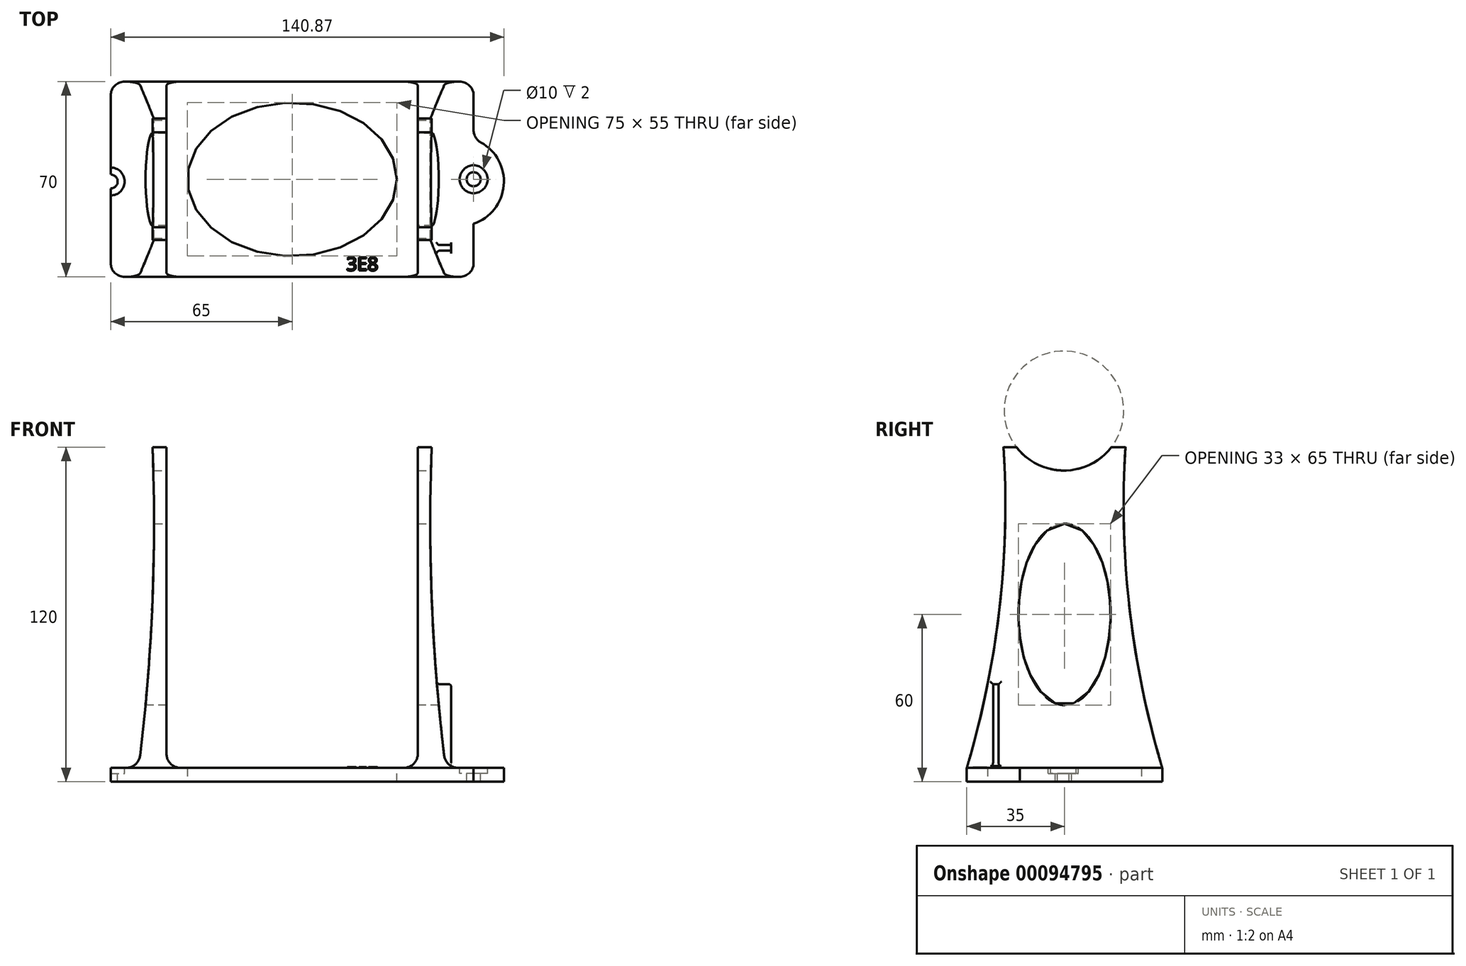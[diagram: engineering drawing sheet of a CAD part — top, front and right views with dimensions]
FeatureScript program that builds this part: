
annotation { "Feature Type Name" : "Feature", "Feature Type Description" : "" }
export const myFeature = defineFeature(function(context is Context, id is Id, definition is map)
    precondition{}
    {
        {
            var Q0;
            Q0=qCreatedBy(makeId("Front.planeOp"),FACE);
            var sketch = newSketch(context, id + "F0", { "sketchPlane" : qUnion([Q0])});
            skLineSegment(sketch, "E0", {"start": v(-65, 0) * mm, "end": v(65, 0) * mm});
            skLineSegment(sketch, "E1", {"start": v(0, 0) * mm, "end": v(0, 120) * mm, "construction": true});
            skLineSegment(sketch, "E2", {"start": v(-65, 0) * mm, "end": v(-65, 5) * mm});
            skLineSegment(sketch, "E3", {"start": v(-65, 5) * mm, "end": v(-55, 5) * mm});
            skLineSegment(sketch, "E4", {"start": v(-45, 120) * mm, "end": v(45, 120) * mm, "construction": true});
            skLineSegment(sketch, "E5", {"start": v(-45, 120) * mm, "end": v(-45, 5) * mm});
            skLineSegment(sketch, "E6", {"start": v(-45, 5) * mm, "end": v(0, 5) * mm});
            skLineSegment(sketch, "E7", {"start": v(-45, 120) * mm, "end": v(-50, 120) * mm});
            skArc(sketch, "E8", {"start": v(-55, 5) * mm, "mid": v(-50.13, 62.4) * mm, "end": v(-50, 120) * mm});
            skLineSegment(sketch, "E9.MirrorCS", {"start": v(45, 5) * mm, "end": v(0, 5) * mm});
            skLineSegment(sketch, "E10.MirrorCS", {"start": v(45, 120) * mm, "end": v(45, 5) * mm});
            skLineSegment(sketch, "E11.MirrorCS", {"start": v(45, 120) * mm, "end": v(50, 120) * mm});
            skArc(sketch, "E12.MirrorCS", {"start": v(55, 5) * mm, "mid": v(50.13, 62.4) * mm, "end": v(50, 120) * mm});
            skLineSegment(sketch, "E13.MirrorCS", {"start": v(65, 5) * mm, "end": v(55, 5) * mm});
            skLineSegment(sketch, "E14.MirrorCS", {"start": v(65, 0) * mm, "end": v(65, 5) * mm});
            skSolve(sketch);
        }
        {
            var Q0;
            Q0 = qSketchRegion(id + "F0", true);
            extrude(context, id + "F1", {"entities" : qUnion([Q0]), "endBound" : BoundingType.SYMMETRIC, "depth" : 70 * mm});
        }
        {
            var Q0;
            Q0=qCreatedBy(makeId("Right.planeOp"),FACE);
            var sketch = newSketch(context, id + "F2", { "sketchPlane" : qUnion([Q0])});
            skLineSegment(sketch, "E15.0", {"start": v(-35, 120) * mm, "end": v(35, 120) * mm, "construction": true});
            skPoint(sketch, "E16", {"position": v(0, 120) * mm});
            skArc(sketch, "E17", {"start": v(-21.63, 132.72) * mm, "mid": v(0.07, 111.58) * mm, "end": v(21.2, 133.28) * mm});
            skLineSegment(sketch, "E18", {"start": v(-0.21, 133) * mm, "end": v(0, 120) * mm, "construction": true});
            skLineSegment(sketch, "E19", {"start": v(21.2, 133.28) * mm, "end": v(-21.63, 132.72) * mm});
            skPoint(sketch, "E20", {"position": v(16.81, 120) * mm});
            skLineSegment(sketch, "E21", {"start": v(16.81, 120) * mm, "end": v(21.81, 120) * mm});
            skPoint(sketch, "E22.0", {"position": v(35, 5) * mm});
            skArc(sketch, "E23", {"start": v(21.81, 120) * mm, "mid": v(23.32, 61.92) * mm, "end": v(35, 5) * mm});
            skLineSegment(sketch, "E24", {"start": v(0, 120) * mm, "end": v(0, 0) * mm, "construction": true});
            skEllipse(sketch, "E25", {"center": v(0, 60) * mm, "majorRadius": 32.5 * mm, "minorRadius": 16.5 * mm, "majorAxis": v(0, 1)});
            skLineSegment(sketch, "E26", {"start": v(21.81, 120) * mm, "end": v(35, 120) * mm});
            skLineSegment(sketch, "E27", {"start": v(35, 120) * mm, "end": v(35, 5) * mm});
            skArc(sketch, "E28.MirrorCS", {"start": v(-21.81, 120) * mm, "mid": v(-23.32, 61.92) * mm, "end": v(-35, 5) * mm});
            skLineSegment(sketch, "E29.MirrorCS", {"start": v(-21.81, 120) * mm, "end": v(-35, 120) * mm});
            skLineSegment(sketch, "E30.MirrorCS", {"start": v(-35, 120) * mm, "end": v(-35, 5) * mm});
            skSolve(sketch);
        }
        {
            var Q0;
            Q0 = qSketchRegion(id + "F2", true);
            extrude(context, id + "F3", {"entities" : qUnion([Q0]), "operationType" : NewBodyOperationType.REMOVE, "endBound" : BoundingType.THROUGH_ALL, "oppositeDirection" : true, "depth" : 25 * mm, "hasSecondDirection" : true, "secondDirectionBound" : SecondDirectionBoundingType.THROUGH_ALL, "secondDirectionOppositeDirection" : false, "secondDirectionDepth" : 25 * mm});
        }
        {
            var Q0;
            Q0=makeQuery(id+"F1.opExtrude","SWEPT_FACE",FACE,{"disambiguationData":[OSD([sQuery(id+"F0.wireOp",EDGE,"E6"),sQuery(id+"F0.wireOp",EDGE,"E9.MirrorCS")])]});
            var sketch = newSketch(context, id + "F4", { "sketchPlane" : qUnion([Q0])});
            skLineSegment(sketch, "E31.0", {"start": v(65, -35) * mm, "end": v(65, 35) * mm, "construction": true});
            skArc(sketch, "E32", {"start": v(65, -15.96) * mm, "mid": v(75.87, -0.8) * mm, "end": v(65, 14.35) * mm});
            skLineSegment(sketch, "E33", {"start": v(65, -15.96) * mm, "end": v(65, 14.35) * mm});
            skPoint(sketch, "E34", {"position": v(65, 0) * mm});
            skLineSegment(sketch, "E35", {"start": v(0, -6.05) * mm, "end": v(0, 5.95) * mm, "construction": true});
            skArc(sketch, "E36.MirrorCS", {"start": v(-65, -15.96) * mm, "mid": v(-75.87, -0.8) * mm, "end": v(-65, 14.35) * mm});
            skLineSegment(sketch, "E37.MirrorCS", {"start": v(-65, -15.96) * mm, "end": v(-65, 14.35) * mm});
            skPoint(sketch, "E38", {"position": v(-65, -0.8) * mm});
            skEllipse(sketch, "E39", {"center": v(0, 0) * mm, "majorRadius": 37.5 * mm, "minorRadius": 27.5 * mm, "majorAxis": v(1, 0)});
            skSolve(sketch);
        }
        {
            var Q0;
            Q0=makeQuery(id+"F4.imprint","IMPRINT",FACE,{"disambiguationData":[TD([[makeQuery(id+"F4.imprint","IMPRINT",EDGE,{"derivedFrom":sQuery(id+"F4.wireOp",EDGE,"E39")}),1.0]])]});
            extrude(context, id + "F5", {"entities" : qUnion([Q0]), "operationType" : NewBodyOperationType.REMOVE, "endBound" : BoundingType.THROUGH_ALL, "oppositeDirection" : true, "depth" : 25 * mm});
        }
        {
            var Q0;
            Q0=makeQuery(id+"F4.imprint","IMPRINT",FACE,{"disambiguationData":[TD([[makeQuery(id+"F4.imprint","IMPRINT",EDGE,{"derivedFrom":sQuery(id+"F4.wireOp",EDGE,"E32")}),1.0]])]});
            var Q1;
            Q1=makeQuery(id+"F4.imprint","IMPRINT",FACE,{"disambiguationData":[TD([[makeQuery(id+"F4.imprint","IMPRINT",EDGE,{"derivedFrom":sQuery(id+"F4.wireOp",EDGE,"E36.MirrorCS")}),-1.0]])]});
            extrude(context, id + "F6", {"entities" : qUnion([Q0, Q1]), "operationType" : NewBodyOperationType.ADD, "oppositeDirection" : true, "depth" : 5 * mm});
        }
        {
            var Q0;
            Q0=sQuery(id+"F4.wireOp",VERTEX,"E34");
            var Q1;
            Q1=sQuery(id+"F4.wireOp",VERTEX,"E38");
            var Q2;
            Q2=makeQuery(id+"F1.opExtrude","SWEPT_BODY",BODY,{"disambiguationData":[OSD([sQuery(id+"F0.wireOp",EDGE,"E0"),sQuery(id+"F0.wireOp",EDGE,"E2"),sQuery(id+"F0.wireOp",EDGE,"E3"),sQuery(id+"F0.wireOp",EDGE,"E5"),sQuery(id+"F0.wireOp",EDGE,"E6"),sQuery(id+"F0.wireOp",EDGE,"E7"),sQuery(id+"F0.wireOp",EDGE,"E8"),sQuery(id+"F0.wireOp",EDGE,"E9.MirrorCS"),sQuery(id+"F0.wireOp",EDGE,"E10.MirrorCS"),sQuery(id+"F0.wireOp",EDGE,"E11.MirrorCS"),sQuery(id+"F0.wireOp",EDGE,"E12.MirrorCS"),sQuery(id+"F0.wireOp",EDGE,"E13.MirrorCS"),sQuery(id+"F0.wireOp",EDGE,"E14.MirrorCS")])]});
            hole(context, id + "F7", {"style" : HoleStyle.C_BORE, "endStyle" : HoleEndStyle.THROUGH, "holeDiameter" : 5 * mm, "cBoreDiameter" : 10 * mm, "cBoreDepth" : 2 * mm, "locations" : qUnion([Q0, Q1]), "scope" : qUnion([Q2]), "isTappedThrough" : true});
        }
        {
            var Q0;
            Q0=makeQuery(id+"F1.opExtrude","CAP_EDGE",EDGE,{"disambiguationData":[OSD([sQuery(id+"F0.wireOp",EDGE,"E14.MirrorCS")])],"isStart":true});
            var Q1;
            Q1=makeQuery(id+"F1.opExtrude","CAP_EDGE",EDGE,{"disambiguationData":[OSD([sQuery(id+"F0.wireOp",EDGE,"E2")])],"isStart":true});
            var Q2;
            Q2=makeQuery(id+"F1.opExtrude","CAP_EDGE",EDGE,{"disambiguationData":[OSD([sQuery(id+"F0.wireOp",EDGE,"E2")])],"isStart":false});
            var Q3;
            Q3=makeQuery(id+"F1.opExtrude","CAP_EDGE",EDGE,{"disambiguationData":[OSD([sQuery(id+"F0.wireOp",EDGE,"E14.MirrorCS")])],"isStart":false});
            var Q4;
            {var subQ0=sQuery(id+"F4.wireOp",EDGE,"E33");var subQ1=sQuery(id+"F4.wireOp",EDGE,"E32");Q4=makeQuery(id+"F6.opExtrude","SWEPT_EDGE",EDGE,{"disambiguationData":[OSD([subQ1,subQ0]),TDD([makeQuery(id+"F4.imprint","INTERSECT",VERTEX,{"disambiguationData":[OD(0.0)],"derivedFrom":[subQ1,subQ0]})])]});}
            var Q5;
            {var subQ0=sQuery(id+"F4.wireOp",EDGE,"E33");var subQ1=sQuery(id+"F4.wireOp",EDGE,"E32");Q5=makeQuery(id+"F6.opExtrude","SWEPT_EDGE",EDGE,{"disambiguationData":[OSD([subQ1,subQ0]),TDD([makeQuery(id+"F4.imprint","INTERSECT",VERTEX,{"disambiguationData":[OD(1.0)],"derivedFrom":[subQ1,subQ0]})])]});}
            var Q6;
            {var subQ0=sQuery(id+"F4.wireOp",EDGE,"E37.MirrorCS");var subQ1=sQuery(id+"F4.wireOp",EDGE,"E36.MirrorCS");Q6=makeQuery(id+"F6.opExtrude","SWEPT_EDGE",EDGE,{"disambiguationData":[OSD([subQ1,subQ0]),TDD([makeQuery(id+"F4.imprint","INTERSECT",VERTEX,{"disambiguationData":[OD(1.0)],"derivedFrom":[subQ1,subQ0]})])]});}
            var Q7;
            {var subQ0=sQuery(id+"F4.wireOp",EDGE,"E37.MirrorCS");var subQ1=sQuery(id+"F4.wireOp",EDGE,"E36.MirrorCS");Q7=makeQuery(id+"F6.opExtrude","SWEPT_EDGE",EDGE,{"disambiguationData":[OSD([subQ1,subQ0]),TDD([makeQuery(id+"F4.imprint","INTERSECT",VERTEX,{"disambiguationData":[OD(0.0)],"derivedFrom":[subQ1,subQ0]})])]});}
            var Q8;
            Q8=makeQuery(id+"F1.opExtrude","SWEPT_EDGE",EDGE,{"disambiguationData":[OSD([sQuery(id+"F0.wireOp",EDGE,"E12.MirrorCS"),sQuery(id+"F0.wireOp",EDGE,"E13.MirrorCS")])]});
            var Q9;
            Q9=makeQuery(id+"F1.opExtrude","SWEPT_EDGE",EDGE,{"disambiguationData":[OSD([sQuery(id+"F0.wireOp",EDGE,"E3"),sQuery(id+"F0.wireOp",EDGE,"E8")])]});
            var Q10;
            Q10=makeQuery(id+"F1.opExtrude","SWEPT_EDGE",EDGE,{"disambiguationData":[OSD([sQuery(id+"F0.wireOp",EDGE,"E9.MirrorCS"),sQuery(id+"F0.wireOp",EDGE,"E10.MirrorCS")])]});
            var Q11;
            Q11=makeQuery(id+"F1.opExtrude","SWEPT_EDGE",EDGE,{"disambiguationData":[OSD([sQuery(id+"F0.wireOp",EDGE,"E5"),sQuery(id+"F0.wireOp",EDGE,"E6")])]});
            fillet(context, id + "F8", {"entities" : qUnion([Q0, Q1, Q2, Q3, Q4, Q5, Q6, Q7, Q8, Q9, Q10, Q11]), "radius" : 5 * mm, "tangentPropagation" : true, "allowEdgeOverflow" : false});
        }
        {
            var Q0;
            Q0=makeQuery(id+"F4.imprint","IMPRINT",FACE,{"disambiguationData":[TD([[makeQuery(id+"F4.imprint","IMPRINT",EDGE,{"derivedFrom":sQuery(id+"F4.wireOp",EDGE,"E39")}),-1.0]])]});
            var sketch = newSketch(context, id + "F9", { "sketchPlane" : qUnion([Q0])});
            skText(sketch, "E40", { "text": "3E8", "fontName": "OpenSans-Regular.ttf"});
            const initialGuessF9  = {"E40": [0.0194, -0.03273, 1, 0, 0.00484]};
            skSetInitialGuess(sketch, initialGuessF9);
            skSolve(sketch);
        }
        {
            var Q0;
            Q0 = qSketchRegion(id + "F9", true);
            extrude(context, id + "F10", {"entities" : qUnion([Q0]), "operationType" : NewBodyOperationType.ADD, "depth" : .3 * mm});
        }
        {
            var Q0;
            Q0=qCreatedBy(makeId("Right.planeOp"),FACE);
            cPlane(context, id + "F11", {"entities" : qUnion([Q0]), "cplaneType" : CPlaneType.OFFSET, "offset" : 57 * mm, "width" : 150 * mm, "height" : 150 * mm});
        }
        {
            var Q0;
            Q0=qCreatedBy(id+"F11.planeOp",FACE);
            var sketch = newSketch(context, id + "F12", { "sketchPlane" : qUnion([Q0])});
            skLineSegment(sketch, "E41.0.1", {"start": v(35, 5) * mm, "end": v(-35, 5) * mm, "construction": true});
            skLineSegment(sketch, "E41.0.3", {"start": v(-35, 5) * mm, "end": v(-30, 5) * mm, "construction": true});
            skLineSegment(sketch, "E41.0.4", {"start": v(-30, 5) * mm, "end": v(-19.2, 5) * mm, "construction": true});
            skLineSegment(sketch, "E41.0.5", {"start": v(-19.2, 5) * mm, "end": v(-14.82, 5) * mm, "construction": true});
            skLineSegment(sketch, "E41.0.6", {"start": v(-14.82, 5) * mm, "end": v(13.21, 5) * mm, "construction": true});
            skLineSegment(sketch, "E41.0.7", {"start": v(13.21, 5) * mm, "end": v(17.6, 5) * mm, "construction": true});
            skLineSegment(sketch, "E41.0.8", {"start": v(17.6, 5) * mm, "end": v(30, 5) * mm, "construction": true});
            skLineSegment(sketch, "E41.0.9", {"start": v(30, 5) * mm, "end": v(35, 5) * mm, "construction": true});
            skLineSegment(sketch, "E42", {"start": v(-35, 5) * mm, "end": v(-24.6, 5) * mm, "construction": true});
            skLineSegment(sketch, "E43", {"start": v(-24.6, 5) * mm, "end": v(-24.6, 20) * mm, "construction": true});
            skLineSegment(sketch, "E44.bottom", {"start": v(-25.6, 5) * mm, "end": v(-23.6, 5) * mm});
            skLineSegment(sketch, "E44.top", {"start": v(-25.6, 35) * mm, "end": v(-23.6, 35) * mm});
            skLineSegment(sketch, "E44.left", {"start": v(-25.6, 5) * mm, "end": v(-25.6, 35) * mm});
            skLineSegment(sketch, "E44.right", {"start": v(-23.6, 5) * mm, "end": v(-23.6, 35) * mm});
            skPoint(sketch, "E44.middle", {"position": v(-24.6, 20) * mm});
            skSolve(sketch);
        }
        {
            var Q0;
            Q0 = qSketchRegion(id + "F12", true);
            extrude(context, id + "F13", {"entities" : qUnion([Q0]), "operationType" : NewBodyOperationType.ADD, "oppositeDirection" : true, "depth" : 5.5 * mm});
        }
        {
            var Q0;
            Q0=makeQuery(id+"F13.opExtrude","CAP_EDGE",EDGE,{"disambiguationData":[OSD([sQuery(id+"F12.wireOp",EDGE,"E44.top")])],"isStart":true});
            var Q1;
            Q1=makeQuery(id+"F13.boolean.opBoolean","INTERSECT",EDGE,{"derivedFrom":[makeQuery(id+"F1.opExtrude","SWEPT_FACE",FACE,{"disambiguationData":[OSD([sQuery(id+"F0.wireOp",EDGE,"E12.MirrorCS")])]}),makeQuery(id+"F13.opExtrude","SWEPT_FACE",FACE,{"disambiguationData":[OSD([sQuery(id+"F12.wireOp",EDGE,"E44.top")])]})]});
            var Q2;
            Q2=makeQuery(id+"F13.boolean.opBoolean","INTERSECT",EDGE,{"derivedFrom":[makeQuery(id+"F1.opExtrude","SWEPT_FACE",FACE,{"disambiguationData":[OSD([sQuery(id+"F0.wireOp",EDGE,"E12.MirrorCS")])]}),makeQuery(id+"F13.opExtrude","SWEPT_FACE",FACE,{"disambiguationData":[OSD([sQuery(id+"F12.wireOp",EDGE,"E44.left")])]})]});
            var Q3;
            Q3=makeQuery(id+"F13.boolean.opBoolean","INTERSECT",EDGE,{"derivedFrom":[makeQuery(id+"F1.opExtrude","SWEPT_FACE",FACE,{"disambiguationData":[OSD([sQuery(id+"F0.wireOp",EDGE,"E12.MirrorCS")])]}),makeQuery(id+"F13.opExtrude","SWEPT_FACE",FACE,{"disambiguationData":[OSD([sQuery(id+"F12.wireOp",EDGE,"E44.right")])]})]});
            fillet(context, id + "F14", {"entities" : qUnion([Q0, Q1, Q2, Q3]), "radius" : 1 * mm, "tangentPropagation" : true, "allowEdgeOverflow" : false});
        }
    });
